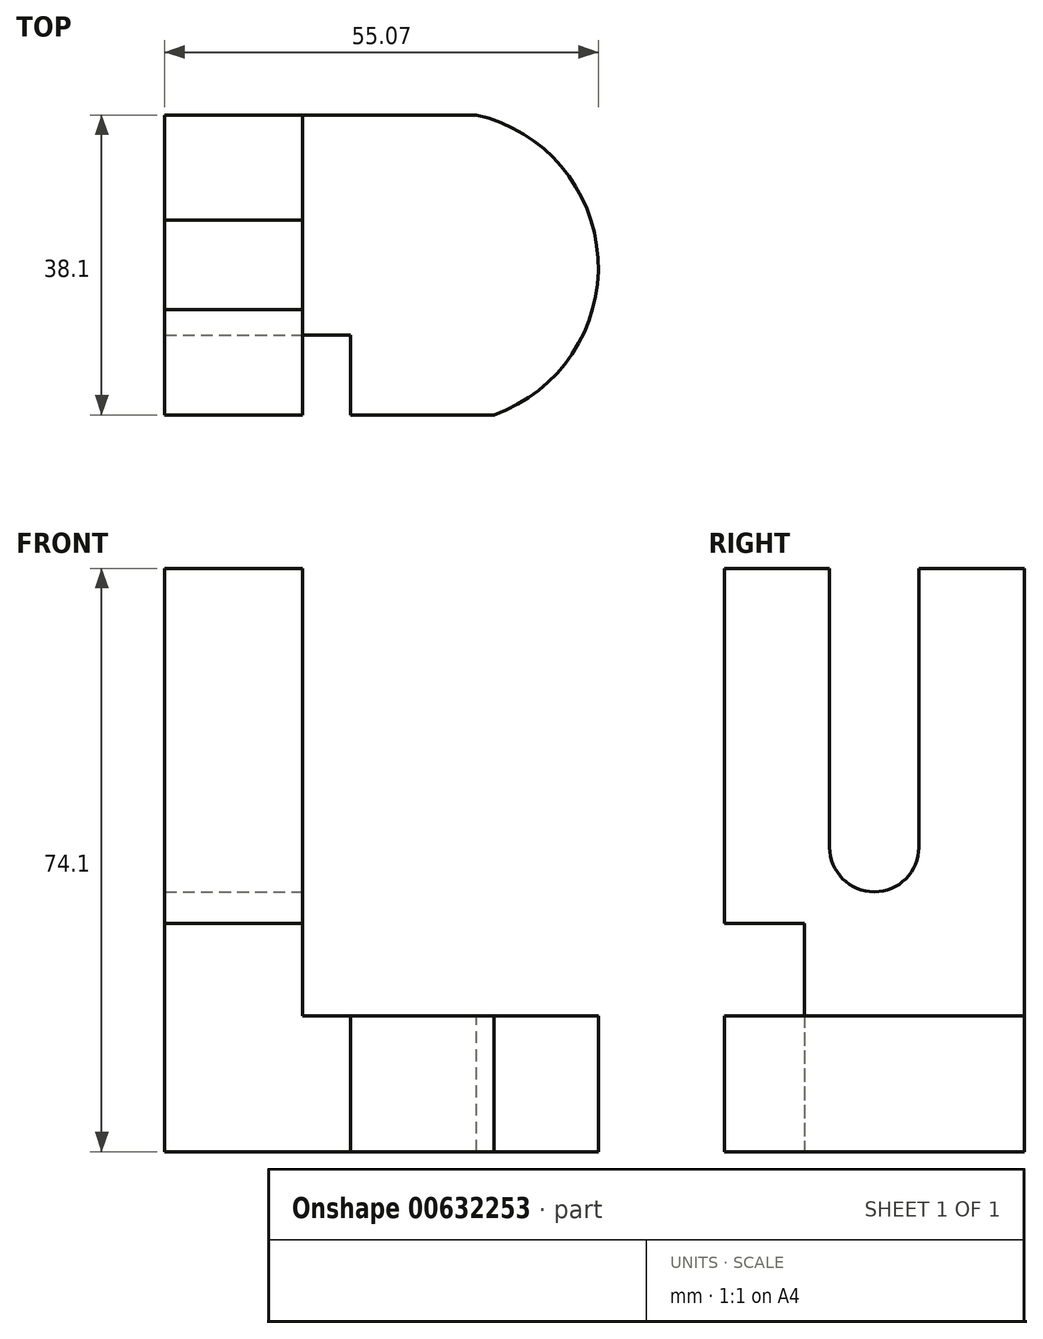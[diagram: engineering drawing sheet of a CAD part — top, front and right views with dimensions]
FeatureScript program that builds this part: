
annotation { "Feature Type Name" : "Feature", "Feature Type Description" : "" }
export const myFeature = defineFeature(function(context is Context, id is Id, definition is map)
    precondition{}
    {
        {
            var Q0;
            Q0=qCreatedBy(makeId("Front.planeOp"),FACE);
            var sketch = newSketch(context, id + "F0", { "sketchPlane" : qUnion([Q0])});
            skLineSegment(sketch, "E0", {"start": v(0, 74.1) * mm, "end": v(0, 0) * mm});
            skLineSegment(sketch, "E1", {"start": v(0, 0) * mm, "end": v(55.07, 0) * mm});
            skLineSegment(sketch, "E2", {"start": v(55.07, 0) * mm, "end": v(55.07, 17.24) * mm});
            skLineSegment(sketch, "E3", {"start": v(55.07, 17.24) * mm, "end": v(17.47, 17.24) * mm});
            skLineSegment(sketch, "E4", {"start": v(17.47, 17.24) * mm, "end": v(17.47, 74.1) * mm});
            skLineSegment(sketch, "E5", {"start": v(17.47, 74.1) * mm, "end": v(0, 74.1) * mm});
            skSolve(sketch);
        }
        {
            var Q0;
            Q0 = qSketchRegion(id + "F0", true);
            extrude(context, id + "F1", {"entities" : qUnion([Q0]), "endBound" : BoundingType.SYMMETRIC, "depth" : 38.1 * mm, "offsetDistance" : 25.4 * mm});
        }
        {
            var Q0;
            Q0=makeQuery(id+"F1.opExtrude","SWEPT_FACE",FACE,{"disambiguationData":[OSD([sQuery(id+"F0.wireOp",EDGE,"E3")])]});
            var sketch = newSketch(context, id + "F2", { "sketchPlane" : qUnion([Q0])});
            skArc(sketch, "E6", {"start": v(41.85, -19.05) * mm, "mid": v(55.03, 0.84) * mm, "end": v(39.6, 19.05) * mm});
            skSolve(sketch);
        }
        {
            var Q0;
            {var subQ0=sQuery(id+"F2.wireOp",EDGE,"E6");Q0=makeQuery(id+"F2.imprint","IMPRINT",FACE,{"disambiguationData":[TD([[makeQuery(id+"F2.imprint","IMPRINT",EDGE,{"derivedFrom":subQ0}),-1.0]])]});}
            extrude(context, id + "F3", {"entities" : qUnion([Q0]), "operationType" : NewBodyOperationType.REMOVE, "endBound" : BoundingType.THROUGH_ALL, "oppositeDirection" : true, "depth" : 25.4 * mm, "offsetDistance" : 25.4 * mm});
        }
        {
            var Q0;
            Q0=makeQuery(id+"F1.opExtrude","SWEPT_FACE",FACE,{"disambiguationData":[OSD([sQuery(id+"F0.wireOp",EDGE,"E4")])]});
            var sketch = newSketch(context, id + "F4", { "sketchPlane" : qUnion([Q0])});
            skLineSegment(sketch, "E7.bottom", {"start": v(-5.67, 74.1) * mm, "end": v(5.67, 74.1) * mm});
            skLineSegment(sketch, "E7.left", {"start": v(-5.67, 74.1) * mm, "end": v(-5.67, 38.68) * mm});
            skLineSegment(sketch, "E7.right", {"start": v(5.67, 74.1) * mm, "end": v(5.67, 38.68) * mm});
            skPoint(sketch, "E7.middle", {"position": v(0, 56.39) * mm});
            skArc(sketch, "E8", {"start": v(-5.67, 38.68) * mm, "mid": v(0, 33) * mm, "end": v(5.67, 38.68) * mm});
            skSolve(sketch);
        }
        {
            var Q0;
            Q0 = qSketchRegion(id + "F4", true);
            extrude(context, id + "F5", {"entities" : qUnion([Q0]), "operationType" : NewBodyOperationType.REMOVE, "oppositeDirection" : true, "depth" : 25.4 * mm, "offsetDistance" : 25.4 * mm});
        }
        {
            var Q0;
            Q0=makeQuery(id+"F1.opExtrude","CAP_FACE",FACE,{"disambiguationData":[OSD([sQuery(id+"F0.wireOp",EDGE,"E0"),sQuery(id+"F0.wireOp",EDGE,"E1"),sQuery(id+"F0.wireOp",EDGE,"E2"),sQuery(id+"F0.wireOp",EDGE,"E3"),sQuery(id+"F0.wireOp",EDGE,"E4"),sQuery(id+"F0.wireOp",EDGE,"E5")])],"isStart":false});
            var sketch = newSketch(context, id + "F6", { "sketchPlane" : qUnion([Q0])});
            skLineSegment(sketch, "E9.bottom", {"start": v(0, 28.97) * mm, "end": v(23.56, 28.97) * mm});
            skLineSegment(sketch, "E9.top", {"start": v(0, -5.2) * mm, "end": v(23.56, -5.2) * mm});
            skLineSegment(sketch, "E9.left", {"start": v(0, 28.97) * mm, "end": v(0, -5.2) * mm});
            skLineSegment(sketch, "E9.right", {"start": v(23.56, 28.97) * mm, "end": v(23.56, -5.2) * mm});
            skSolve(sketch);
        }
        {
            var Q0;
            Q0 = qSketchRegion(id + "F6", true);
            extrude(context, id + "F7", {"entities" : qUnion([Q0]), "operationType" : NewBodyOperationType.REMOVE, "oppositeDirection" : true, "depth" : 10.16 * mm, "offsetDistance" : 25.4 * mm});
        }
    });
